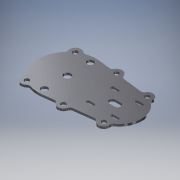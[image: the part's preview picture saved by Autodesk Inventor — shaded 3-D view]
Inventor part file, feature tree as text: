
AUTODESK INVENTOR PART (.ipt)
format: ipt  version: 2017 (Build 210142000, 142)  size: 304,128 bytes
history: native  units: mm
features: extrude x4, sketch x4, other x1, fillet x1
ambient origin geometry x8: Origin, YZ Plane, XZ Plane, XY Plane, X Axis, Y Axis, Z Axis, Center Point
bodies: Body1 (feature_tree)
feature tree (10):
  other  "Sólido1"
  extrude  "Extrusión1"  Depth=88.9mm
  extrude  "Extrusión2"  Depth=22.225mm
  fillet  "Empalme1"  Radius=22.225mm
  extrude  "Extrusión3"  Depth=22.225mm
  extrude  "Extrusión4"  TaperAngle=0.0deg  [1 undecoded]
  sketch  "Boceto1"  dims[d0=114.3mm d1=88.9mm]
  sketch  "Boceto2"  dims[d2=203.2mm d3=22.225mm d4=22.225mm]
  sketch  "Boceto3"  dims[d7=22.225mm d8=22.225mm]
  sketch  "Boceto4"  dims[d11=22.225mm d13=0.0mm d14=22.225mm d16=4.445mm d17=0.0mm d18=9.525mm d19=9.525mm d20=9.525mm d21=9.525mm d22=9.525mm d23=9.525mm d24=25.4mm d25=0.0mm d26=6.35mm d27=12.7mm d28=12.7mm d29=44.45mm d30=44.45mm d31=31.75mm d32=31.75mm d33=14.2875mm d34=12.7mm d35=12.7mm d36=45.0mm d37=45.0mm d38=25.4mm d39=0.0mm d40=12.7mm d41=56.0mm d42=56.0mm d43=28.0mm d44=28.0mm d45=0.0mm d46=93.4212mm d47=47.5mm d48=47.5mm d49=23.75mm d50=23.75mm d57=5.55625mm d58=5.159375mm d59=5.55625mm d60=5.55625mm d61=5.159375mm d62=5.159375mm d63=5.55625mm d64=5.159375mm d65=0.0mm d66=5.55625mm d67=5.55625mm d68=5.159375mm d69=5.159375mm d70=0.0mm d71=5.55625mm d72=5.55625mm d73=5.159375mm d74=5.159375mm d75=0.0mm d76=25.4mm d77=0.0mm d78=12.7mm d79=12.7mm d80=5.159375mm d81=5.159375mm]
note: 1 required parameter value undecoded (feature->parameter linkage not recoverable at this tier; creation-order binding heuristic only, values carry confidence <= 0.55)
